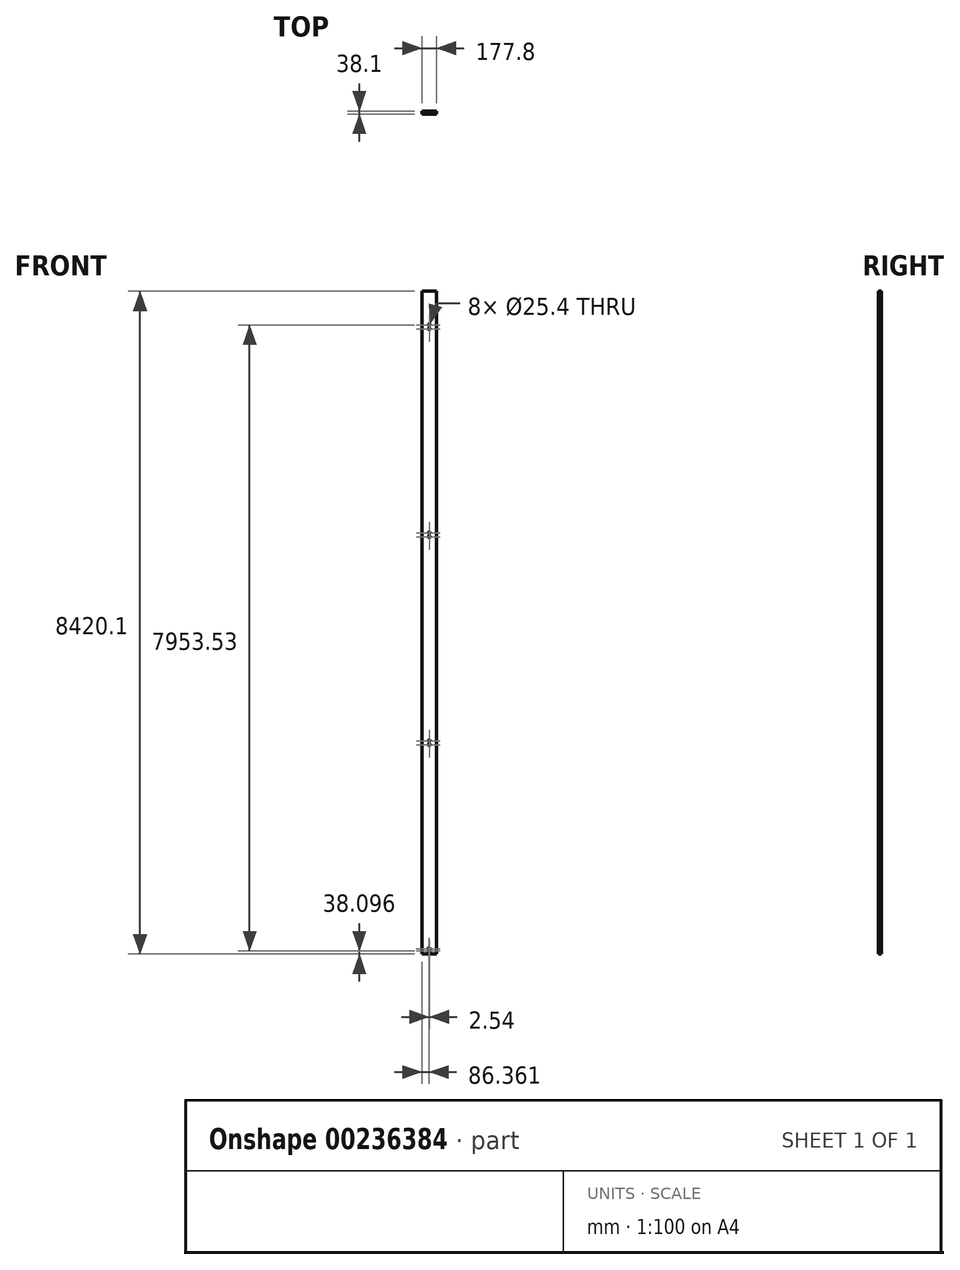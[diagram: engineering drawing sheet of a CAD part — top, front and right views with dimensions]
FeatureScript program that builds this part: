
annotation { "Feature Type Name" : "Feature", "Feature Type Description" : "" }
export const myFeature = defineFeature(function(context is Context, id is Id, definition is map)
    precondition{}
    {
        {
            var Q0;
            Q0=qCreatedBy(makeId("Front.planeOp"),FACE);
            var sketch = newSketch(context, id + "F0", { "sketchPlane" : qUnion([Q0])});
            skLineSegment(sketch, "E0.bottom", {"start": v(-508.63, 6462.69) * mm, "end": v(-330.83, 6462.69) * mm});
            skLineSegment(sketch, "E0.top", {"start": v(-508.63, -1957.41) * mm, "end": v(-330.83, -1957.41) * mm});
            skLineSegment(sketch, "E0.left", {"start": v(-508.63, 6462.69) * mm, "end": v(-508.63, -1957.41) * mm});
            skLineSegment(sketch, "E0.right", {"start": v(-330.83, 6462.69) * mm, "end": v(-330.83, -1957.41) * mm});
            skCircle(sketch, "E1", {"center": v(-419.73, -1919.31) * mm, "radius": 12.7 * mm});
            skCircle(sketch, "E2", {"center": v(-422.27, -1890.58) * mm, "radius": 12.7 * mm});
            skCircle(sketch, "E3", {"center": v(-419.73, 700.22) * mm, "radius": 12.7 * mm});
            skCircle(sketch, "E4", {"center": v(-419.73, 751.02) * mm, "radius": 12.7 * mm});
            skCircle(sketch, "E5", {"center": v(-419.73, 3341.82) * mm, "radius": 12.7 * mm});
            skCircle(sketch, "E6", {"center": v(-419.73, 5983.42) * mm, "radius": 12.7 * mm});
            skCircle(sketch, "E7", {"center": v(-419.73, 3392.62) * mm, "radius": 12.7 * mm});
            skCircle(sketch, "E8", {"center": v(-419.73, 6034.22) * mm, "radius": 12.7 * mm});
            skSolve(sketch);
        }
        {
            var Q0;
            Q0=makeQuery(id+"F0.imprint","IMPRINT",FACE,{"disambiguationData":[TD([[makeQuery(id+"F0.imprint","IMPRINT",EDGE,{"derivedFrom":sQuery(id+"F0.wireOp",EDGE,"E0.bottom")}),-1.0]])]});
            extrude(context, id + "F1", {"entities" : qUnion([Q0]), "depth" : 38.1 * mm});
        }
    });
